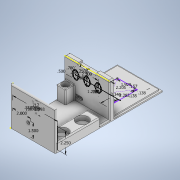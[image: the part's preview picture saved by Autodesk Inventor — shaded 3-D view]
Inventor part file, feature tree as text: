
AUTODESK INVENTOR PART (.ipt)
format: ipt  version: 2020 (Build 240168000, 168)  size: 415,744 bytes
history: native  units: in
note: dims shown in document units (in); Inventor stores cm internally (conversion verified against a paired STEP export)
features: sketch x15, extrude x12, hole x4, fillet x3, projected_geometry x1
ambient origin geometry x8: Origin, YZ Plane, XZ Plane, XY Plane, X Axis, Y Axis, Z Axis, Center Point
bodies: Solid1 (feature_tree)
feature tree (35):
  extrude  "Extrusion1"  Depth=4.0in
  sketch  "Sketch2"  dims[d2=0.5in d3=0.0in d4=1.25in]
  extrude  "Extrusion4"  Depth=1.25in
  extrude  "Extrusion5"  Depth=2.5in
  sketch  "Sketch5"  dims[d12=0.25in d13=0.5in]
  hole  "Hole1"  [1 undecoded]
  extrude  "Extrusion9"  Depth=0.5in
  extrude  "Extrusion10"  Depth=0.3937in
  extrude  "Extrusion11"  Depth=6.0in TaperAngle=0.0deg
  sketch  "Sketch13"  dims[d27=0.25in d28=4.0in d29=0.0in]
  extrude  "Extrusion12"  Depth=4.0in TaperAngle=0.0deg
  hole  "Hole2"  [1 undecoded]
  extrude  "Extrusion13"  TaperAngle=90.0deg  [1 undecoded]
  extrude  "Extrusion14"  Depth=0.333in
  hole  "Hole3"  [1 undecoded]
  fillet  "Fillet1"  Radius=1.5in
  fillet  "Fillet2"  Radius=5.0in
  sketch  "Sketch17"  dims[d36=0.712in]
  extrude  "Extrusion15"  Depth=1.3in
  hole  "Hole4"  [1 undecoded]
  extrude  "Extrusion16"  Depth=0.0625in TaperAngle=0.0deg
  extrude  "Extrusion17"  Depth=0.0625in
  fillet  "Fillet3"  Radius=2.2047in
  sketch  "Sketch1"  dims[d0=5.0in d1=4.0in]
  sketch  "Sketch3"  dims[d5=1.25in d6=2.5in]
  sketch  "Sketch4"  dims[d7=0.78in d9=0.78in]
  sketch  "Sketch10"  dims[d14=1.1811in d16=1.25in d17=0.3937in d19=1.0in d23=5.0in]
  sketch  "Sketch12"  dims[d24=0.25in d25=6.0in d26=0.0in]
  sketch  "Sketch14"  dims[d30=5.0in d31=2.25in]
  sketch  "Sketch15"  dims[d32=1.293in d33=90.0deg]
  sketch  "Sketch16"  dims[d34=0.356in d35=0.333in]
  sketch  "Sketch18"  dims[d37=0.134in d38=0.75in d39=0.256in d40=0.118in d41=0.5635in d42=1.0in d43=0.8108in d58=1.0in d59=1.5in d60=5.0in]
  sketch  "Sketch19"  dims[d61=0.75in d62=0.0in d69=1.3in]
  sketch  "Sketch20"  dims[d70=1.3in d71=0.5in d72=0.0in d73=5.4in d74=0.0in d75=3.3465in d76=2.2047in d77=0.1378in d78=0.1378in d79=0.1575in d80=0.7874in d82=1.9291in d83=0.7874in d85=2.2835in d88=0.125in d89=0.0in d90=0.0793in d91=0.197in d92=0.217in d93=0.098in d94=0.5635in d95=0.299in d96=0.8108in d97=0.2in d98=5.0in d99=0.2in d100=0.2in d101=0.125in d102=0.0in d103=0.3in d104=2.0in d105=0.2in d106=0.0in d107=0.196in d108=0.25in d109=0.217in d110=0.098in d111=0.5635in d112=0.25in d113=0.8108in d114=0.125in d115=1.25in d116=90.0deg d117=1.25in d118=90.0deg d119=0.125in d120=2.0in d121=1.5in d122=0.35in d123=0.75in d124=0.375in d125=0.25in d126=0.5635in d127=0.5in d128=0.0in d129=1.0in d130=1.0in d131=1.5in d132=0.0in d133=0.5in d134=0.5in d135=90.0deg d136=0.78in d137=1.0in d138=0.0in d139=1.0in d140=0.25in d141=1.25in d142=0.0in d143=1.0in d144=0.25in d145=0.25in d146=0.0625in]
  projected_geometry  "Projected Loop1"
note: 5 required parameter values undecoded (feature->parameter linkage not recoverable at this tier; creation-order binding heuristic only, values carry confidence <= 0.55)
